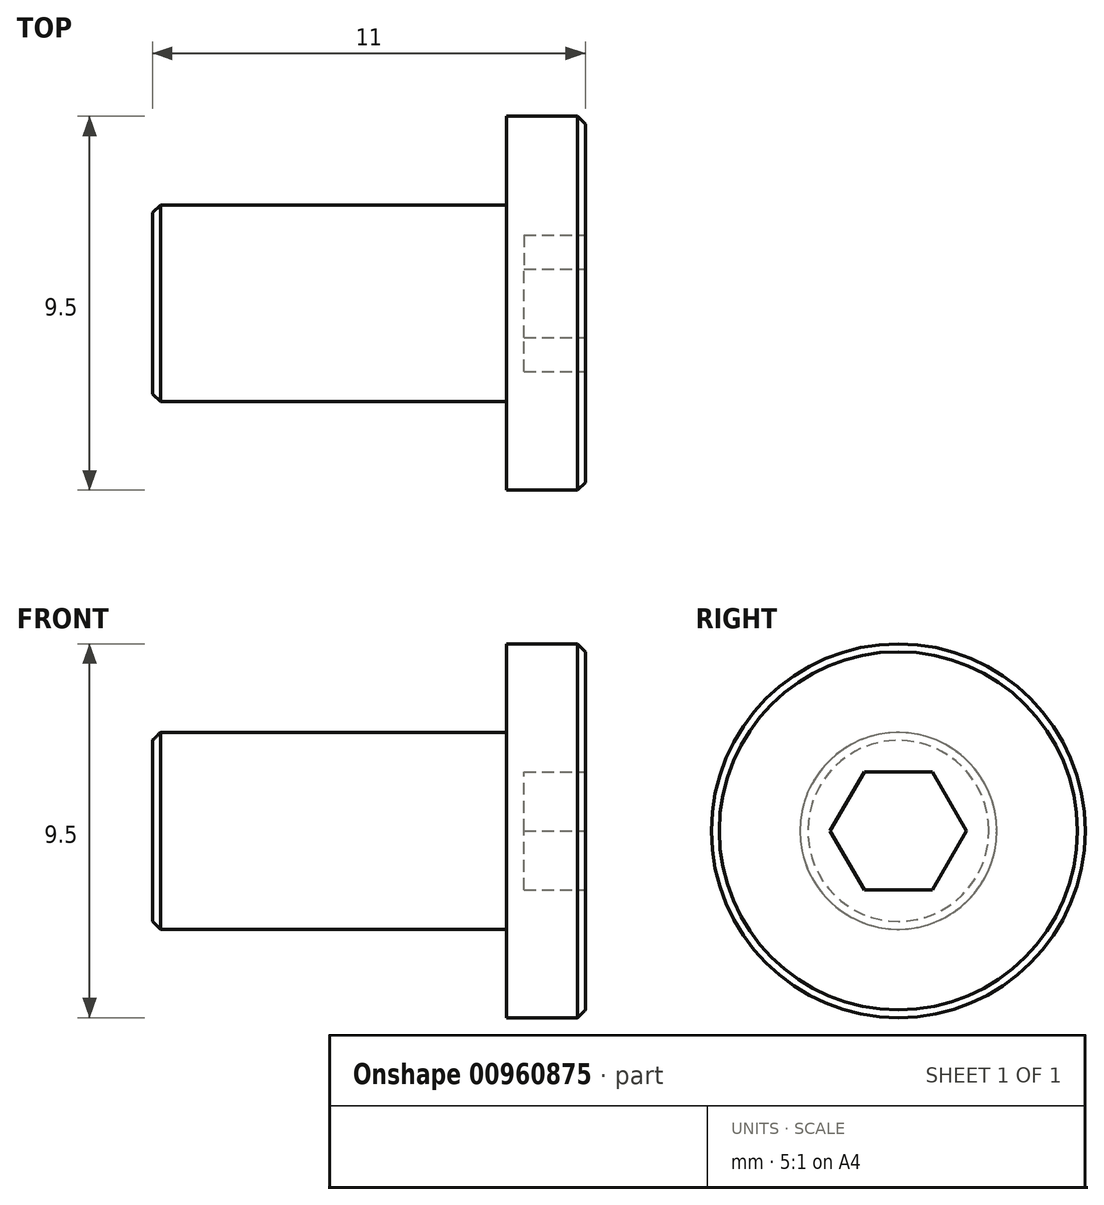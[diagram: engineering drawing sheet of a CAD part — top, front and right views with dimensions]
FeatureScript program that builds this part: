
annotation { "Feature Type Name" : "Feature", "Feature Type Description" : "" }
export const myFeature = defineFeature(function(context is Context, id is Id, definition is map)
    precondition{}
    {
        {
            var Q0;
            Q0=qCreatedBy(makeId("Front.planeOp"),FACE);
            var sketch = newSketch(context, id + "F0", { "sketchPlane" : qUnion([Q0])});
            skLineSegment(sketch, "E0.bottom", {"start": v(4.04, 36) * mm, "end": v(-4.96, 36) * mm});
            skLineSegment(sketch, "E0.top", {"start": v(4.04, 33.5) * mm, "end": v(-4.96, 33.5) * mm});
            skLineSegment(sketch, "E0.left", {"start": v(4.04, 36) * mm, "end": v(4.04, 33.5) * mm});
            skLineSegment(sketch, "E0.right", {"start": v(-4.96, 36) * mm, "end": v(-4.96, 33.5) * mm});
            skLineSegment(sketch, "E1.bottom", {"start": v(4.04, 33.5) * mm, "end": v(6.04, 33.5) * mm});
            skLineSegment(sketch, "E1.top", {"start": v(4.04, 38.26) * mm, "end": v(6.04, 38.26) * mm});
            skLineSegment(sketch, "E1.left", {"start": v(4.04, 33.5) * mm, "end": v(4.04, 38.26) * mm});
            skLineSegment(sketch, "E1.right", {"start": v(6.04, 33.5) * mm, "end": v(6.04, 38.26) * mm});
            skSolve(sketch);
        }
        {
            var Q0;
            Q0 = qSketchRegion(id + "F0", true);
            var Q1;
            Q1=sQuery(id+"F0.wireOp",EDGE,"E0.top");
            revolve(context, id + "F1", {"surfaceOperationType" : NewSurfaceOperationType.NEW, "entities" : qUnion([Q0]), "axis" : qUnion([Q1]), "revolveType" : RevolveType.FULL});
        }
        {
            var Q0;
            Q0=makeQuery(id+"F1.opRevolve","SWEPT_EDGE",EDGE,{"disambiguationData":[OSD([sQuery(id+"F0.wireOp",EDGE,"E0.bottom"),sQuery(id+"F0.wireOp",EDGE,"E0.right")])]});
            var Q1;
            Q1=makeQuery(id+"F1.opRevolve","SWEPT_EDGE",EDGE,{"disambiguationData":[OSD([sQuery(id+"F0.wireOp",EDGE,"E1.top"),sQuery(id+"F0.wireOp",EDGE,"E1.right")])]});
            chamfer(context, id + "F2", {"entities" : qUnion([Q0, Q1]), "width" : 0.2 * mm, "tangentPropagation" : true});
        }
        {
            var Q0;
            Q0=makeQuery(id+"F1.opRevolve","SWEPT_FACE",FACE,{"disambiguationData":[OSD([sQuery(id+"F0.wireOp",EDGE,"E1.right")])]});
            var sketch = newSketch(context, id + "F3", { "sketchPlane" : qUnion([Q0])});
            skCircle(sketch, "E2.cCircle", {"center": v(0, 33.5) * mm, "radius": 1.5 * mm, "construction": true});
            skLineSegment(sketch, "E2.0", {"start": v(-0.87, 35) * mm, "end": v(0.87, 35) * mm});
            skLineSegment(sketch, "E2.1", {"start": v(0.87, 35) * mm, "end": v(1.73, 33.5) * mm});
            skLineSegment(sketch, "E2.2", {"start": v(1.73, 33.5) * mm, "end": v(0.87, 32) * mm});
            skLineSegment(sketch, "E2.3", {"start": v(0.87, 32) * mm, "end": v(-0.87, 32) * mm});
            skLineSegment(sketch, "E2.4", {"start": v(-0.87, 32) * mm, "end": v(-1.73, 33.5) * mm});
            skLineSegment(sketch, "E2.5", {"start": v(-1.73, 33.5) * mm, "end": v(-0.87, 35) * mm});
            skPoint(sketch, "E2.0.midPoint", {"position": v(0, 35) * mm});
            skSolve(sketch);
        }
        {
            var Q0;
            Q0 = qSketchRegion(id + "F3", true);
            extrude(context, id + "F4", {"entities" : qUnion([Q0]), "operationType" : NewBodyOperationType.REMOVE, "oppositeDirection" : true, "depth" : 1.56 * mm, "offsetDistance" : 25 * mm});
        }
    });
